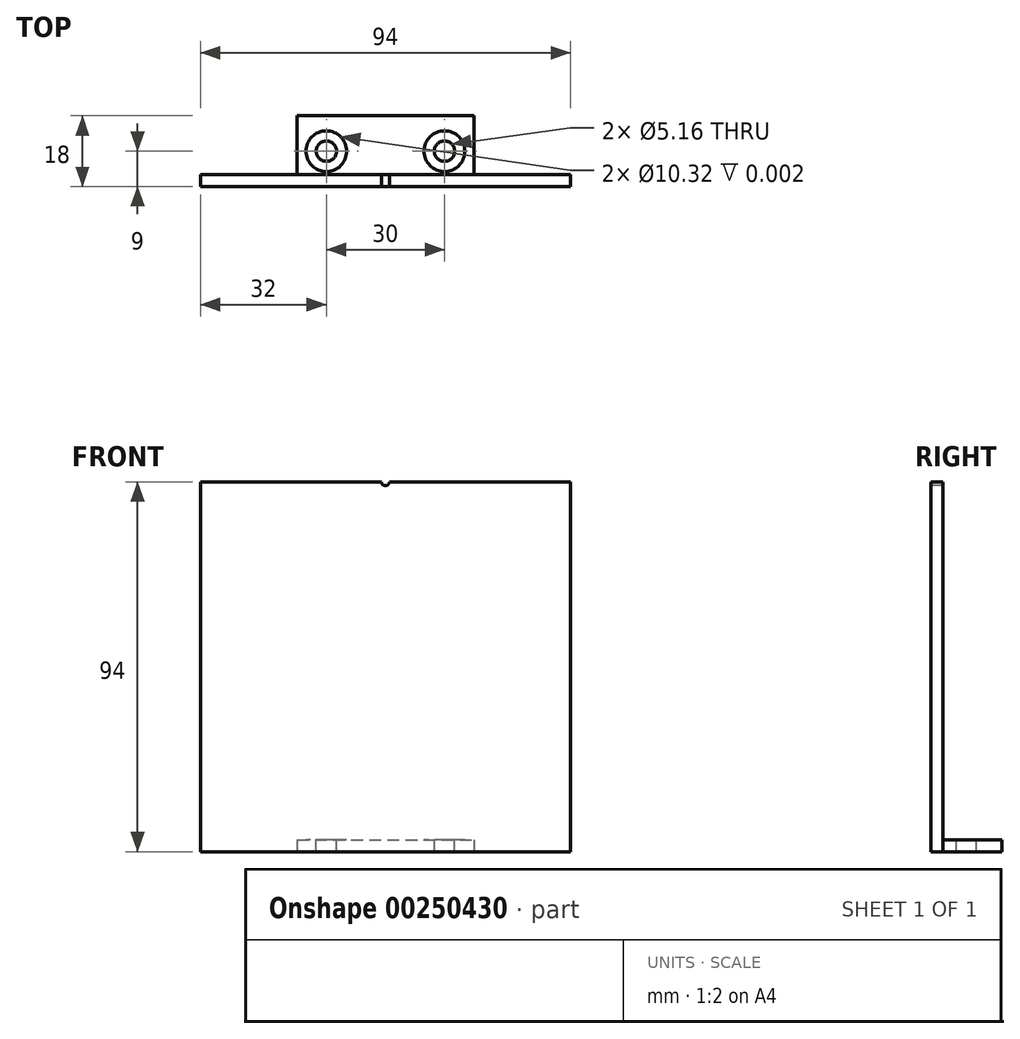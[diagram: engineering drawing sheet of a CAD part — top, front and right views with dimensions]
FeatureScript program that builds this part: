
annotation { "Feature Type Name" : "Feature", "Feature Type Description" : "" }
export const myFeature = defineFeature(function(context is Context, id is Id, definition is map)
    precondition{}
    {
        {
            var Q0;
            Q0=qCreatedBy(makeId("Front.planeOp"),FACE);
            var sketch = newSketch(context, id + "F0", { "sketchPlane" : qUnion([Q0])});
            skLineSegment(sketch, "E0.bottom", {"start": v(-47, 47) * mm, "end": v(47, 47) * mm});
            skLineSegment(sketch, "E0.top", {"start": v(-47, -47) * mm, "end": v(47, -47) * mm});
            skLineSegment(sketch, "E0.left", {"start": v(-47, 47) * mm, "end": v(-47, -47) * mm});
            skLineSegment(sketch, "E0.right", {"start": v(47, 47) * mm, "end": v(47, -47) * mm});
            skLineSegment(sketch, "E1.bottom", {"start": v(-50, 50) * mm, "end": v(50, 50) * mm, "construction": true});
            skLineSegment(sketch, "E1.top", {"start": v(-50, -50) * mm, "end": v(50, -50) * mm, "construction": true});
            skLineSegment(sketch, "E1.left", {"start": v(-50, 50) * mm, "end": v(-50, -50) * mm, "construction": true});
            skLineSegment(sketch, "E1.right", {"start": v(50, 50) * mm, "end": v(50, -50) * mm, "construction": true});
            skSolve(sketch);
        }
        {
            var Q0;
            Q0=qSketchRegion(id+"F0",true);
            extrude(context, id + "F1", {"entities" : qUnion([Q0]), "depth" : 3 * mm});
        }
        {
            var Q0;
            Q0=makeQuery(id+"F1.opExtrude","SWEPT_FACE",FACE,{"disambiguationData":[OSD([sQuery(id+"F0.wireOp",EDGE,"E0.top")])]});
            var sketch = newSketch(context, id + "F2", { "sketchPlane" : qUnion([Q0])});
            skLineSegment(sketch, "E2.0", {"start": v(-22.5, 0) * mm, "end": v(22.5, 0) * mm});
            skLineSegment(sketch, "E3", {"start": v(-22.5, 0) * mm, "end": v(-22.5, -15) * mm});
            skLineSegment(sketch, "E4", {"start": v(-22.5, -15) * mm, "end": v(22.5, -15) * mm});
            skLineSegment(sketch, "E5", {"start": v(22.5, -15) * mm, "end": v(22.5, 0) * mm});
            skPoint(sketch, "E6.orphan", {"position": v(-47, 0) * mm});
            skPoint(sketch, "E7.orphan", {"position": v(47, 0) * mm});
            skSolve(sketch);
        }
        {
            var Q0;
            Q0=makeQuery(id+"F2.imprint","IMPRINT",FACE,{"disambiguationData":[TD([[makeQuery(id+"F2.imprint","IMPRINT",EDGE,{"derivedFrom":sQuery(id+"F2.wireOp",EDGE,"E2.0")}),-1.0]])]});
            extrude(context, id + "F3", {"entities" : qUnion([Q0]), "operationType" : NewBodyOperationType.ADD, "oppositeDirection" : true, "depth" : 3 * mm});
        }
        {
            var Q0;
            Q0=makeQuery(id+"F3.opExtrude","CAP_FACE",FACE,{"disambiguationData":[OSD([sQuery(id+"F2.wireOp",EDGE,"E2.0"),sQuery(id+"F2.wireOp",EDGE,"E3"),sQuery(id+"F2.wireOp",EDGE,"E4"),sQuery(id+"F2.wireOp",EDGE,"E5")])],"isStart":false});
            var sketch = newSketch(context, id + "F4", { "sketchPlane" : qUnion([Q0])});
            skCircle(sketch, "E8", {"center": v(-15, 6) * mm, "radius": 2.58 * mm});
            skCircle(sketch, "E9", {"center": v(15, 6) * mm, "radius": 2.58 * mm});
            skSolve(sketch);
        }
        {
            var Q0;
            Q0 = qSketchRegion(id + "F4", true);
            extrude(context, id + "F5", {"entities" : qUnion([Q0]), "operationType" : NewBodyOperationType.REMOVE, "endBound" : BoundingType.THROUGH_ALL, "oppositeDirection" : true, "depth" : 25 * mm});
        }
        {
            var Q0;
            Q0=makeQuery(id+"F3.opExtrude","CAP_FACE",FACE,{"disambiguationData":[OSD([sQuery(id+"F2.wireOp",EDGE,"E2.0"),sQuery(id+"F2.wireOp",EDGE,"E3"),sQuery(id+"F2.wireOp",EDGE,"E4"),sQuery(id+"F2.wireOp",EDGE,"E5")])],"isStart":false});
            var sketch = newSketch(context, id + "F6", { "sketchPlane" : qUnion([Q0])});
            skCircle(sketch, "E10", {"center": v(-15, 6) * mm, "radius": 5.16 * mm});
            skCircle(sketch, "E11", {"center": v(15, 6) * mm, "radius": 5.16 * mm});
            skSolve(sketch);
        }
        {
            var Q0;
            Q0 = qSketchRegion(id + "F6", true);
            extrude(context, id + "F7", {"entities" : qUnion([Q0]), "operationType" : NewBodyOperationType.REMOVE, "oppositeDirection" : true, "depth" : 1 / 406.4 * mm});
        }
        {
            var Q0;
            Q0=makeQuery(id+"F1.opExtrude","CAP_FACE",FACE,{"disambiguationData":[OSD([sQuery(id+"F0.wireOp",EDGE,"E0.bottom"),sQuery(id+"F0.wireOp",EDGE,"E0.top"),sQuery(id+"F0.wireOp",EDGE,"E0.left"),sQuery(id+"F0.wireOp",EDGE,"E0.right")])],"isStart":false});
            var sketch = newSketch(context, id + "F8", { "sketchPlane" : qUnion([Q0])});
            skCircle(sketch, "E12", {"center": v(0, 47) * mm, "radius": 1 * mm});
            skSolve(sketch);
        }
        {
            var Q0;
            Q0 = qSketchRegion(id + "F8", true);
            extrude(context, id + "F9", {"entities" : qUnion([Q0]), "operationType" : NewBodyOperationType.REMOVE, "endBound" : BoundingType.THROUGH_ALL, "oppositeDirection" : true, "depth" : 25 * mm});
        }
    });
